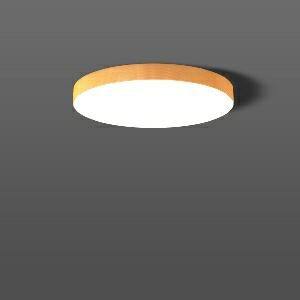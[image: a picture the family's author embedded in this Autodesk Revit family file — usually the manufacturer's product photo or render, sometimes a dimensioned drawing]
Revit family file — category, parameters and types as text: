
# Revit family: flatliner_slim_312285_002_76_fd79
name_source: partatom
category: Lighting Fixtures
units: mm (PartAtom-declared; Revit-internal decimal feet)

## family parameters
Cut with Voids When Loaded = No
Host = Face
Light Source = No
Part Type = Normal
Room Calculation Point = No
Round Connector Dimension = Use Diameter
Shared = No

## types (1)
- 982558.002 (1 x LED Modul 830, 2750 lm, 3000)
    Apparent Load = 38 VA
    CIE Flux Codes = 45 76 94 95 100
    Color Rendering = 80
    Color Temperature = 3000
    Default Elevation = 1800 mm
    Description = Series: FLATLINER SLIM
Decorative ceiling luminaire for interior decoration. Base luminaire prepared for the installation of fabric lampshade. Base: metal, white, powder-coated. TouchDim sensor capable. Light and/or presence sensors can be integrated. Modular design: with the basic luminaire, a cylindrical fabric lampshade with a polycarbonate satin-finish diffuser must always be ordered separately. Fabric lampshade and diffuser can be assembled without the use of tools. 
Colour: white
Diameter: 496 mm
Height: 34 mm
Lamp: LED exchangeable
Socket: without socket
Colour temperature: 3000K
Colour rendering index (CRI): 83
System power: 38 W
Rated luminous flux: 2750 lm
Beam angle Down: 117°
Luminous efficiency: 72 lm/W
Control gear: AC power, DALI dimmable
Protection class: I
Type of protection: IP 20
    Height = 34 mm  [stored 0.111549 ft]
    Lamp = 1 x LED Modul 830
    Lamp Light Flux = 2750 lm
    Lamp count = 1
    Length = 496 mm
    Lifetime = 50000 h
    Luminous efficacy = 72 lm/W
    Manufacturer = RZB
    ModVariant = No
    Model = 312285.002.76
    Mounting Place = Ceiling
    Mounting Type = Surface mounted
    Number of Poles = 1
    OnlyDefault = Yes
    Power Factor = 1
    Product Name = FLATLINER SLIM
    Product group = Surface mounted ceiling Fabric lampshade luminaires
    ProductGroupID = 313
    Protection Class = Protection class I
    Protection Degree = IP 20
    RLX_Detail_Level = 1
    RLX_Emergency_Light_Flux = 0 lm
    RLX_Emergency_Type = 0
    RLX_Emergency_Type_DB = No
    RlxData = <blob elided: 25429 chars, md5=4aaec4fa>
    Socket = socket
    Standby Power = 0 W
    System Light Flux = 2750 lm
    System Power = 38 W
    Type Image = 312287.002_982442.0063_982444.002.jpg
    URL = http://relux.com
    VarID = 982558_002_dd09
    Voltage = 230 V
    Voltage Range = 220-240 V
    Weight = 0.00 kg
    Width = 0 mm  [stored 0 ft]

note: [stored X ft] marks values corroborated as IEEE doubles in the binary element streams (Revit-internal decimal feet)

## geometry (parser evidence)
native form markers: Blend x4, Sweep x14
no freeform markers — native parametric forms only
